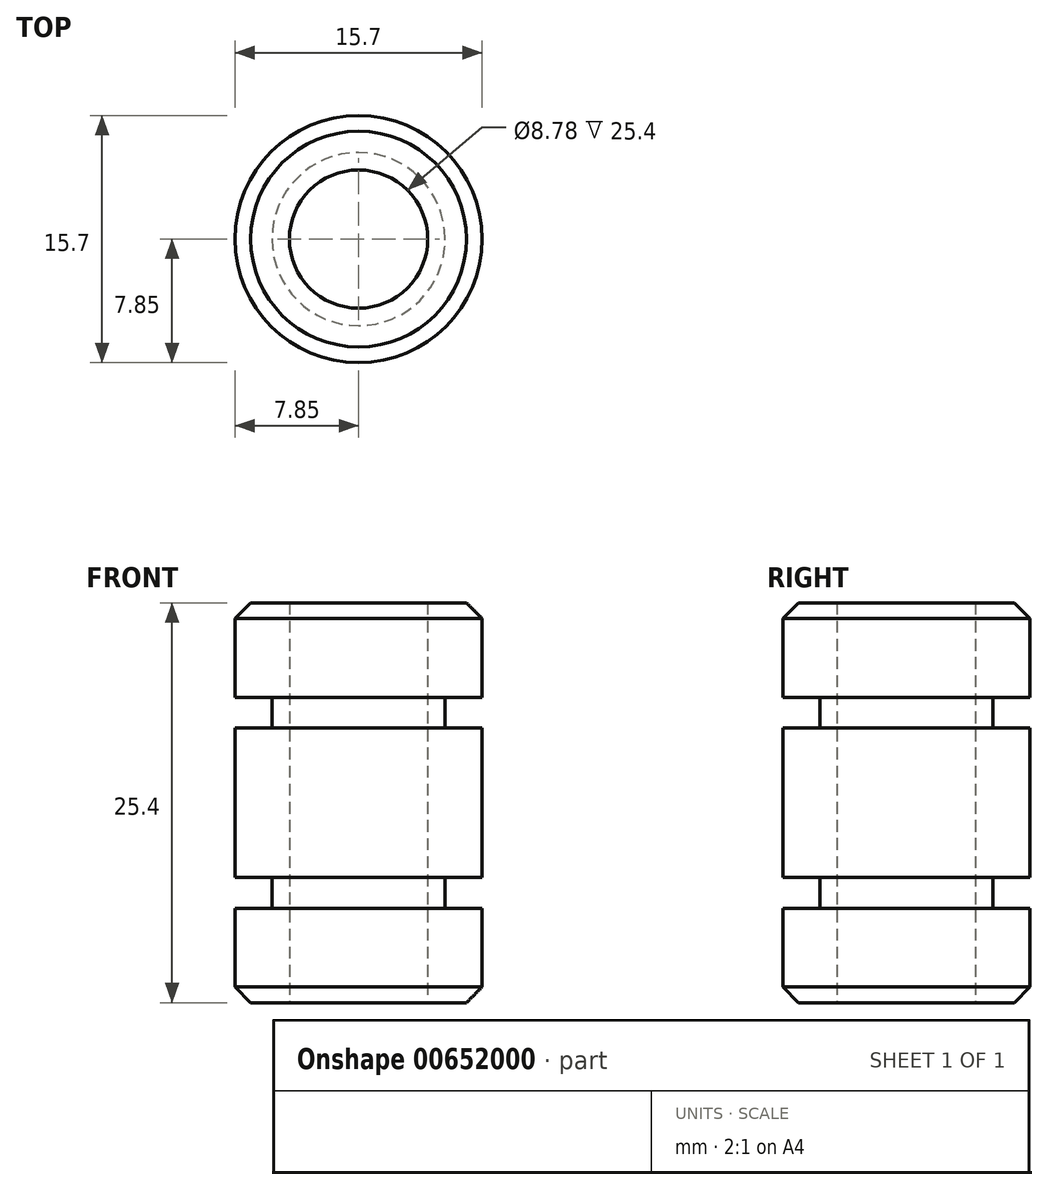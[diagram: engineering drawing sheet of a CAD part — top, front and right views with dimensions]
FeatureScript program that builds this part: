
annotation { "Feature Type Name" : "Feature", "Feature Type Description" : "" }
export const myFeature = defineFeature(function(context is Context, id is Id, definition is map)
    precondition{}
    {
        {
            var Q0;
            Q0=qCreatedBy(makeId("Top.planeOp"),FACE);
            var sketch = newSketch(context, id + "F0", { "sketchPlane" : qUnion([Q0])});
            skCircle(sketch, "E0", {"center": v(0, 0) * mm, "radius": 7.85 * mm});
            skCircle(sketch, "E1", {"center": v(0, 0) * mm, "radius": 4.4 * mm});
            skSolve(sketch);
        }
        {
            var Q0;
            Q0=makeQuery(id+"F0.imprint","IMPRINT",FACE,{"disambiguationData":[TD([[makeQuery(id+"F0.imprint","IMPRINT",EDGE,{"derivedFrom":sQuery(id+"F0.wireOp",EDGE,"E0")}),1.0]])]});
            extrude(context, id + "F1", {"entities" : qUnion([Q0]), "depth" : 6 * mm, "offsetDistance" : 25 * mm});
        }
        {
            var Q0;
            Q0=makeQuery(id+"F1.opExtrude","CAP_FACE",FACE,{"disambiguationData":[OSD([sQuery(id+"F0.wireOp",EDGE,"E0"),sQuery(id+"F0.wireOp",EDGE,"E1")])],"isStart":false});
            var sketch = newSketch(context, id + "F2", { "sketchPlane" : qUnion([Q0])});
            skCircle(sketch, "E2", {"center": v(0, 0) * mm, "radius": 5.5 * mm});
            skCircle(sketch, "E3", {"center": v(0, 0) * mm, "radius": 4.4 * mm});
            skSolve(sketch);
        }
        {
            var Q0;
            Q0=makeQuery(id+"F2.imprint","IMPRINT",FACE,{"disambiguationData":[TD([[makeQuery(id+"F2.imprint","IMPRINT",EDGE,{"derivedFrom":sQuery(id+"F2.wireOp",EDGE,"E2")}),1.0]])]});
            extrude(context, id + "F3", {"entities" : qUnion([Q0]), "operationType" : NewBodyOperationType.ADD, "depth" : 1.95 * mm, "offsetDistance" : 25 * mm});
        }
        {
            var Q0;
            Q0=makeQuery(id+"F3.opExtrude","CAP_FACE",FACE,{"disambiguationData":[OSD([sQuery(id+"F2.wireOp",EDGE,"E2"),sQuery(id+"F2.wireOp",EDGE,"E3")])],"isStart":false});
            var sketch = newSketch(context, id + "F4", { "sketchPlane" : qUnion([Q0])});
            skCircle(sketch, "E4", {"center": v(0, 0) * mm, "radius": 7.85 * mm});
            skCircle(sketch, "E5", {"center": v(0, 0) * mm, "radius": 4.4 * mm});
            skSolve(sketch);
        }
        {
            var Q0;
            Q0=makeQuery(id+"F4.imprint","IMPRINT",FACE,{"disambiguationData":[TD([[makeQuery(id+"F4.imprint","IMPRINT",EDGE,{"derivedFrom":sQuery(id+"F4.wireOp",EDGE,"E4")}),1.0]])]});
            extrude(context, id + "F5", {"entities" : qUnion([Q0]), "depth" : 9.5 * mm, "offsetDistance" : 25 * mm});
        }
        {
            var Q0;
            Q0=makeQuery(id+"F3.opExtrude","CAP_FACE",FACE,{"disambiguationData":[OSD([sQuery(id+"F2.wireOp",EDGE,"E2"),sQuery(id+"F2.wireOp",EDGE,"E3")])],"isStart":false});
            extrude(context, id + "F6", {"entities" : qUnion([Q0]), "depth" : 9.5 * mm, "offsetDistance" : 25 * mm});
        }
        {
            var Q0;
            Q0=makeQuery(id+"F1.opExtrude","SWEPT_BODY",BODY,{"disambiguationData":[OSD([sQuery(id+"F0.wireOp",EDGE,"E0"),sQuery(id+"F0.wireOp",EDGE,"E1")])]});
            var Q1;
            Q1=makeQuery(id+"F5.opExtrude","SWEPT_BODY",BODY,{"disambiguationData":[OSD([sQuery(id+"F2.wireOp",EDGE,"E2"),sQuery(id+"F4.wireOp",EDGE,"E4")])]});
            var Q2;
            Q2=makeQuery(id+"F6.opExtrude","SWEPT_BODY",BODY,{"disambiguationData":[OSD([sQuery(id+"F2.wireOp",EDGE,"E2"),sQuery(id+"F2.wireOp",EDGE,"E3")])]});
            booleanBodies(context, id + "F7", {"operationType" : BooleanOperationType.UNION, "tools" : qUnion([Q0, Q1, Q2])});
        }
        {
            var Q0;
            {var subQ0=sQuery(id+"F2.wireOp",EDGE,"E2");Q0=makeQuery(id+"F7.opBoolean","MERGE",FACE,{"derivedFrom":[makeQuery(id+"F5.opExtrude","CAP_FACE",FACE,{"disambiguationData":[OSD([subQ0,sQuery(id+"F4.wireOp",EDGE,"E4")])],"isStart":false}),makeQuery(id+"F6.opExtrude","CAP_FACE",FACE,{"disambiguationData":[OSD([subQ0,sQuery(id+"F2.wireOp",EDGE,"E3")])],"isStart":false})]});}
            var sketch = newSketch(context, id + "F8", { "sketchPlane" : qUnion([Q0])});
            skCircle(sketch, "E6", {"center": v(0, 0) * mm, "radius": 5.5 * mm});
            skSolve(sketch);
        }
        {
            var Q0;
            Q0=makeQuery(id+"F8.imprint","IMPRINT",FACE,{"disambiguationData":[TD([[makeQuery(id+"F8.imprint","IMPRINT",EDGE,{"derivedFrom":sQuery(id+"F8.wireOp",EDGE,"E6")}),1.0]])]});
            extrude(context, id + "F9", {"entities" : qUnion([Q0]), "operationType" : NewBodyOperationType.ADD, "depth" : 1.95 * mm, "offsetDistance" : 25 * mm});
        }
        {
            var Q0;
            Q0=makeQuery(id+"F9.opExtrude","CAP_FACE",FACE,{"disambiguationData":[OSD([sQuery(id+"F2.wireOp",EDGE,"E3"),sQuery(id+"F8.wireOp",EDGE,"E6")])],"isStart":false});
            var sketch = newSketch(context, id + "F10", { "sketchPlane" : qUnion([Q0])});
            skCircle(sketch, "E7", {"center": v(0, 0) * mm, "radius": 7.85 * mm});
            skCircle(sketch, "E8", {"center": v(0, 0) * mm, "radius": 4.4 * mm});
            skSolve(sketch);
        }
        {
            var Q0;
            Q0=makeQuery(id+"F10.imprint","IMPRINT",FACE,{"disambiguationData":[TD([[makeQuery(id+"F10.imprint","IMPRINT",EDGE,{"derivedFrom":sQuery(id+"F10.wireOp",EDGE,"E8")}),-1.0]])]});
            var Q1;
            Q1=makeQuery(id+"F10.imprint","IMPRINT",FACE,{"disambiguationData":[TD([[makeQuery(id+"F10.imprint","IMPRINT",EDGE,{"derivedFrom":sQuery(id+"F10.wireOp",EDGE,"E7")}),1.0]])]});
            extrude(context, id + "F11", {"entities" : qUnion([Q0, Q1]), "operationType" : NewBodyOperationType.ADD, "depth" : 6 * mm, "offsetDistance" : 25 * mm});
        }
        {
            var Q0;
            Q0=makeQuery(id+"F11.opExtrude","CAP_EDGE",EDGE,{"disambiguationData":[OSD([sQuery(id+"F10.wireOp",EDGE,"E7")])],"isStart":false});
            chamfer(context, id + "F12", {"entities" : qUnion([Q0]), "width" : 1 * mm, "tangentPropagation" : true});
        }
        {
            var Q0;
            Q0=makeQuery(id+"F1.opExtrude","CAP_EDGE",EDGE,{"disambiguationData":[OSD([sQuery(id+"F0.wireOp",EDGE,"E0")])],"isStart":true});
            chamfer(context, id + "F13", {"entities" : qUnion([Q0]), "width" : 1 * mm, "tangentPropagation" : true});
        }
    });
